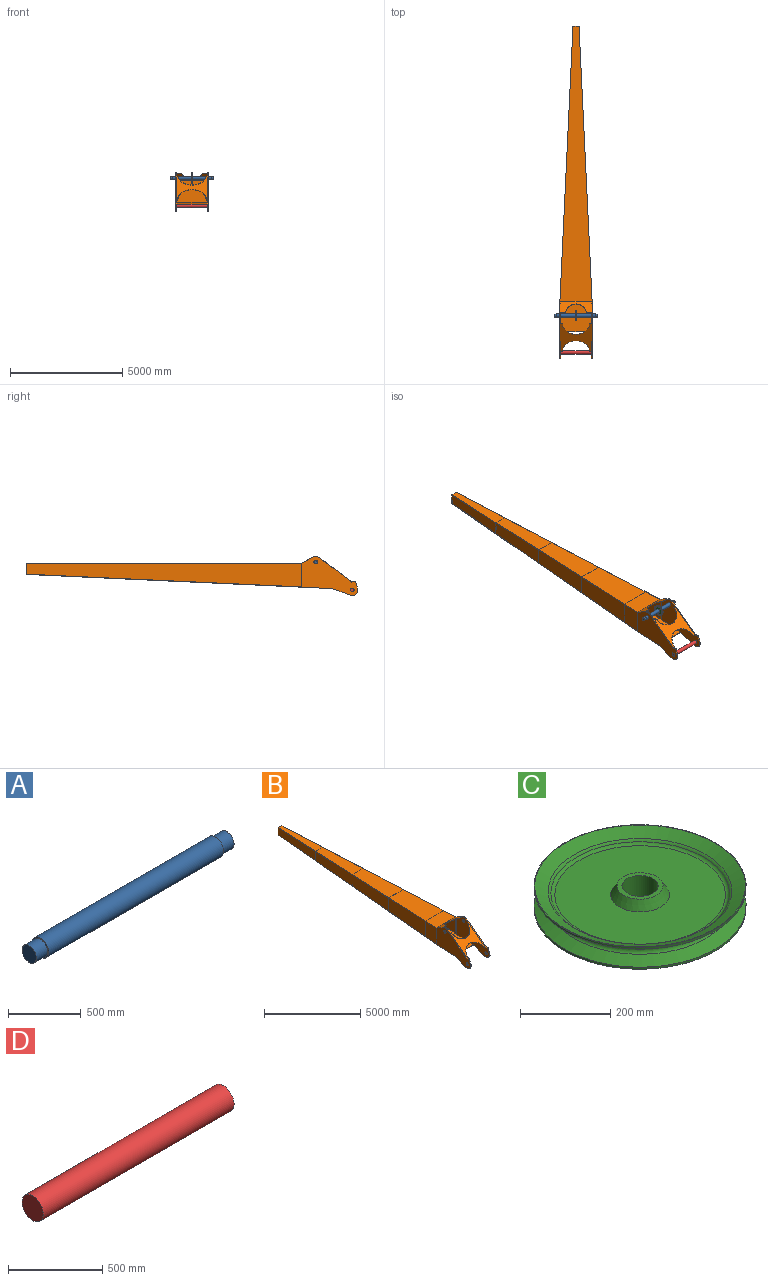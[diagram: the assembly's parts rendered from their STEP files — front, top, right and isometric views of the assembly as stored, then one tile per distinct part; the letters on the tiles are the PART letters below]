
ASSEMBLY  parts=4 mates=4
PART A: 7 faces, bbox 1924.9x160x160 mm
  f0: cylinder r=80mm len=1704.9mm, axis (1,0,0), area 856977mm2, adj f2,f5
  f1: cylinder r=70mm len=140mm, axis (1,0,0), area 48380.5mm2, adj f2,f3
  f2: plane 160x160mm, normal (1,0,0), area 4712.4mm2, adj f0,f1
  f3: plane 140x140mm, normal (1,0,0), area 15393.8mm2, adj f1
  f4: cylinder r=70mm len=140mm, axis (-1,0,0), area 48380.5mm2, adj f5,f6
  f5: plane 160x160mm, normal (-1,0,0), area 4712.4mm2, adj f0,f4
  f6: plane 140x140mm, normal (-1,0,0), area 15393.8mm2, adj f4
PART B: 78 faces, bbox 1433.2x14762.6x1735.9 mm
  f0: plane 266.6x10.34mm, normal (0,-0.86,0.51), area 3199.2mm2, adj f1,f22,f25,f51,f59
  f1: plane 1413.2x512.06mm, normal (0,-0.51,-0.86), area 490131.9mm2, adj f0,f2,f10,f21,f23,f38,f39,f57
  f2: plane 1017.01x0.01mm, normal (0,-1,0), area 0mm2, adj f1,f4,f39
  f3: plane 1413.2x1344.79mm, normal (0,-0.05,1), area 1825325.3mm2, adj f12,f17,f38,f39,f57,f58
  f4: plane 1017.01x850mm, normal (-1,-0.05,0), area 848682.1mm2, adj f2,f10,f12,f28
  f5: plane 2901x525.64mm, normal (0,0,-1), area 1125065.5mm2, adj f7,f9,f18,f27
  f6: plane 2901x525.64mm, normal (0,-0.05,1), area 1126271.6mm2, adj f9,f14,f18,f27
  f7: plane 462.02x270.02mm, normal (0,1,0), area 12250.4mm2, adj f5,f8,f9,f13,f14,f18,f19
  f8: plane 12242x1029.03mm, normal (1,0.05,0), area 9136963.2mm2, adj f7,f11,f13,f16
  f9: plane 2901x584.37mm, normal (-1,-0.05,0), area 1502038.3mm2, adj f5,f6,f7,f27
  f10: plane 1413.18x850mm, normal (0,0,-1), area 1166877.8mm2, adj f1,f4,f20,f28
  f11: plane 12242.56x581.59mm, normal (1,0.05,0), area 147191.6mm2, adj f8,f14,f15,f16
  f12: plane 1413.19x850mm, normal (0,-0.05,1), area 1168130.4mm2, adj f3,f4,f20,f28
  f13: plane 12242x1433.2mm, normal (0,0,1), area 10425434.8mm2, adj f7,f8,f19,f24
  f14: plane 270.02x11.99mm, normal (0,1,0.05), area 3240.3mm2, adj f6,f7,f11,f15,f26
  f15: plane 13586.79x1433.2mm, normal (0,0.05,-1), area 12366031.6mm2, adj f11,f14,f16,f17,f25,f26
  f16: plane 2520.55x1735.94mm, normal (1,0,0), area 2448370.8mm2, adj f8,f11,f15,f17,f22,f23,f24,f29
  f17: plane 1433.2x11.99mm, normal (0,-1,-0.05), area 17198.4mm2, adj f3,f15,f16,f25,f31,f50
  f18: plane 2901x584.37mm, normal (1,-0.05,0), area 1502038.3mm2, adj f5,f6,f7,f27
  f19: plane 12242x1029.03mm, normal (-1,0.05,0), area 9136896mm2, adj f7,f13,f25,f26
  f20: plane 1017.01x850mm, normal (1,-0.05,0), area 848682.1mm2, adj f10,f12,f21,f28
  f21: plane 1017.01x0.01mm, normal (0,-1,0), area 0mm2, adj f1,f20,f58
  f22: plane 1433.2x496.58mm, normal (0,0.51,0.86), area 507731.6mm2, adj f0,f16,f23,f24,f25,f59
  f23: plane 266.6x10.34mm, normal (0,-0.86,0.51), area 3199.2mm2, adj f1,f16,f22,f32,f59
  f24: plane 1433.2x9.4mm, normal (0,0.62,0.78), area 17198.4mm2, adj f13,f16,f22,f25
  f25: plane 2520.55x1735.94mm, normal (-1,0,0), area 2448357mm2, adj f0,f15,f17,f19,f22,f24,f26,f41
  f26: plane 12242.56x581.59mm, normal (-1,0.05,0), area 147158.7mm2, adj f14,f15,f19,f25
  f27: plane 584.36x525.64mm, normal (0,1,0), area 307165.4mm2, adj f5,f6,f9,f18
  f28: plane 1332.42x977.64mm, normal (0,-1,0), area 1302623.1mm2, adj f4,f10,f12,f20
  f29: plane 266.23x89.56mm, normal (0,-0.95,0.32), area 11235.7mm2, adj f16,f30,f36,f38
  f30: cylinder r=250mm len=335.51mm, axis (1,0,0), area 22443.7mm2, adj f16,f29,f31,f38
  f31: plane 839.71x305.63mm, normal (0,0.34,-0.94), area 35743.8mm2, adj f16,f17,f30,f38
  f32: cylinder r=250mm len=277.79mm, axis (1,0,0), area 11804mm2, adj f16,f23,f33,f38
  f33: plane 199.26x150.98mm, normal (0,-0.6,0.8), area 10000mm2, adj f16,f32,f38,f42
  f34: plane 138.1x40mm, normal (0,0.2,0.98), area 5642.1mm2, adj f16,f36,f38,f43
  f35: cylinder r=80mm len=160mm, axis (1,0,0), area 20106.2mm2, adj f16,f38
  f36: cylinder r=50mm len=57.57mm, axis (1,0,0), area 2902.5mm2, adj f16,f29,f34,f38
  f37: cylinder r=80mm len=160mm, axis (1,0,0), area 20106.2mm2, adj f16,f38
  f38: plane 2400x1735.94mm, normal (-1,0,0), area 2279967.2mm2, adj f1,f3,f29,f30,f31,f32,f33,f34
  f39: plane 1093.2x120mm, normal (-0.97,0.24,0), area 130506.5mm2, adj f1,f2,f3,f38
  f40: plane 1353.2x1232.61mm, normal (0,0.6,-0.8), area 974516.4mm2, adj f38,f42,f43,f44,f45,f46,f47,f57
  f41: plane 1433.2x1232.61mm, normal (0,-0.6,0.8), area 1098235.6mm2, adj f16,f25,f42,f43,f44,f45,f46,f47
  f42: plane 120x9.56mm, normal (0,0.8,0.6), area 1440mm2, adj f16,f33,f40,f41,f44
  f43: plane 120x9.56mm, normal (0,-0.8,-0.6), area 1440mm2, adj f16,f34,f40,f41,f45
  f44: cylinder r=596.6mm len=1193.2mm, axis (0,-0.6,0.8), area 22491.3mm2, adj f40,f41,f42,f46
  f45: cylinder r=596.6mm len=1193.2mm, axis (0,-0.6,0.8), area 22491.3mm2, adj f40,f41,f43,f47
  f46: plane 120x9.56mm, normal (0,0.8,0.6), area 1440mm2, adj f25,f40,f41,f44,f52
  f47: plane 120x9.56mm, normal (0,-0.8,-0.6), area 1440mm2, adj f25,f40,f41,f45,f53
  f48: plane 266.23x89.56mm, normal (0,-0.95,0.32), area 11235.7mm2, adj f25,f49,f55,f57
  f49: cylinder r=250mm len=335.51mm, axis (-1,0,0), area 22443.7mm2, adj f25,f48,f50,f57
  f50: plane 839.71x305.63mm, normal (0,0.34,-0.94), area 35743.8mm2, adj f17,f25,f49,f57
  f51: cylinder r=250mm len=277.79mm, axis (-1,0,0), area 11804mm2, adj f0,f25,f52,f57
  f52: plane 199.26x150.98mm, normal (0,-0.6,0.8), area 10000mm2, adj f25,f46,f51,f57
  f53: plane 138.1x40mm, normal (0,0.2,0.98), area 5642.1mm2, adj f25,f47,f55,f57
  f54: cylinder r=80mm len=160mm, axis (-1,0,0), area 20106.2mm2, adj f25,f57
  f55: cylinder r=50mm len=57.57mm, axis (-1,0,0), area 2902.5mm2, adj f25,f48,f53,f57
  f56: cylinder r=80mm len=160mm, axis (-1,0,0), area 20106.2mm2, adj f25,f57
  f57: plane 2400x1735.94mm, normal (1,0,0), area 2279967.2mm2, adj f1,f3,f40,f48,f49,f50,f51,f52
  f58: plane 1093.2x120mm, normal (0.97,0.24,0), area 130507mm2, adj f1,f3,f21,f57
  f59: cylinder r=450mm len=900mm, axis (0,0.51,0.86), area 16964.6mm2, adj f0,f1,f22,f23
  f60: plane 1331.47x977.18mm, normal (0,1,0), area 1301077.5mm2, adj f61,f63,f64,f65
  f61: plane 2817x977.18mm, normal (1,-0.05,0), area 2571831.8mm2, adj f60,f62,f63,f64
  f62: plane 1063.81x846.7mm, normal (0,-1,0), area 900728.4mm2, adj f61,f63,f64,f65
  f63: plane 2817x1331.47mm, normal (0,-0.05,1), area 3377358.8mm2, adj f60,f61,f62,f65
  f64: plane 2817x1331.47mm, normal (0,0,-1), area 3373742mm2, adj f60,f61,f62,f65
  f65: plane 2817x977.18mm, normal (-1,-0.05,0), area 2571831.8mm2, adj f60,f62,f63,f64
  f66: plane 1062.86x846.24mm, normal (0,1,0), area 899431.7mm2, adj f67,f69,f70,f71
  f67: plane 2817x846.24mm, normal (1,-0.05,0), area 2202565.2mm2, adj f66,f68,f69,f70
  f68: plane 795.2x715.77mm, normal (0,-1,0), area 569175.6mm2, adj f67,f69,f70,f71
  f69: plane 2817x1062.86mm, normal (0,-0.05,1), area 2619877mm2, adj f66,f67,f68,f71
  f70: plane 2817x1062.86mm, normal (0,0,-1), area 2617071.4mm2, adj f66,f67,f68,f71
  f71: plane 2817x846.24mm, normal (-1,-0.05,0), area 2202565.2mm2, adj f66,f68,f69,f70
  f72: plane 794.25x715.3mm, normal (0,1,0), area 568127.6mm2, adj f73,f75,f76,f77
  f73: plane 2817x715.3mm, normal (1,-0.05,0), area 1833298.6mm2, adj f72,f74,f75,f76
  f74: plane 584.83x526.59mm, normal (0,-1,0), area 307964.5mm2, adj f73,f75,f76,f77
  f75: plane 2817x794.25mm, normal (0,-0.05,1), area 1862395.3mm2, adj f72,f73,f74,f77
  f76: plane 2817x794.25mm, normal (0,0,-1), area 1860400.9mm2, adj f72,f73,f74,f77
  f77: plane 2817x715.3mm, normal (-1,-0.05,0), area 1833298.6mm2, adj f72,f74,f75,f76
PART C: 20 faces, bbox 470x470x60 mm
  f0: cylinder r=40mm len=80mm, axis (0,0,1), area 15079.6mm2, adj f1,f11
  f1: plane 102x102mm, normal (0,0,-1), area 3144.7mm2, adj f0,f2
  f2: cone r=51mm half-angle=30deg, axis (0,0,1), area 10322.5mm2, adj f1,f3
  f3: plane 378x378mm, normal (0,0,-1), area 98888.3mm2, adj f2,f4
  f4: torus R=189mm, axis (0,0,1), area 12417.1mm2, adj f3,f5
  f5: torus R=211mm, axis (0,0,1), area 9521.3mm2, adj f4,f6
  f6: cone r=233.69mm half-angle=63.1deg, axis (0,0,-1), area 46425.9mm2, adj f5,f7
  f7: plane 470x470mm, normal (0,0,-1), area 1935.5mm2, adj f6,f8
  f8: cylinder r=235mm len=470mm, axis (0,0,1), area 8121mm2, adj f7,f9
  f9: cone r=235mm half-angle=63.1deg, axis (0,0,-1), area 45008.2mm2, adj f8,f10
  f10: torus R=211mm, axis (0,0,1), area 30773.4mm2, adj f9,f19
  f11: plane 102x102mm, normal (0,0,1), area 3144.7mm2, adj f0,f12
  f12: cone r=51mm half-angle=30deg, axis (0,0,-1), area 10322.5mm2, adj f11,f13
  f13: plane 378x378mm, normal (0,0,1), area 98888.3mm2, adj f12,f14
  f14: torus R=189mm, axis (0,0,-1), area 12417.1mm2, adj f13,f15
  f15: torus R=211mm, axis (0,0,-1), area 9521.3mm2, adj f14,f16
  f16: cone r=233.69mm half-angle=63.1deg, axis (0,0,1), area 46425.9mm2, adj f15,f17
  f17: plane 470x470mm, normal (0,0,1), area 1935.5mm2, adj f16,f18
  f18: cylinder r=235mm len=470mm, axis (0,0,-1), area 8121mm2, adj f17,f19
  f19: cone r=235mm half-angle=63.1deg, axis (0,0,1), area 45008.2mm2, adj f10,f18
PART D: 3 faces, bbox 1433.2x160x160 mm
  f0: plane 160x160mm, normal (-1,0,0), area 20106.2mm2, adj f2
  f1: plane 160x160mm, normal (1,0,0), area 20106.2mm2, adj f2
  f2: cylinder r=80mm len=1433.2mm, axis (1,0,0), area 720405.7mm2, adj f0,f1
PLACE A t=(-245.85,0,0)mm
PLACE B at identity fixed
PLACE C rot(axis=(0,1,0),90deg) t=(908.89,303.34,335.94)mm
PLACE D at identity
MATE fastened C.f0 <-> A.f0  axis (1,0,0) through (0,1851.51,335.94)mm
MATE cylindrical A.f0 <-> B.f32  axis (1,0,0) through (852.45,1851.51,335.94)mm
MATE fastened D.f2 <-> B.f30  axis (1,0,0) through (716.6,220.39,-900)mm
MATE planar A.f0 <-> D.f2  axis (1,0,0) through (0,1851.51,335.94)mm
